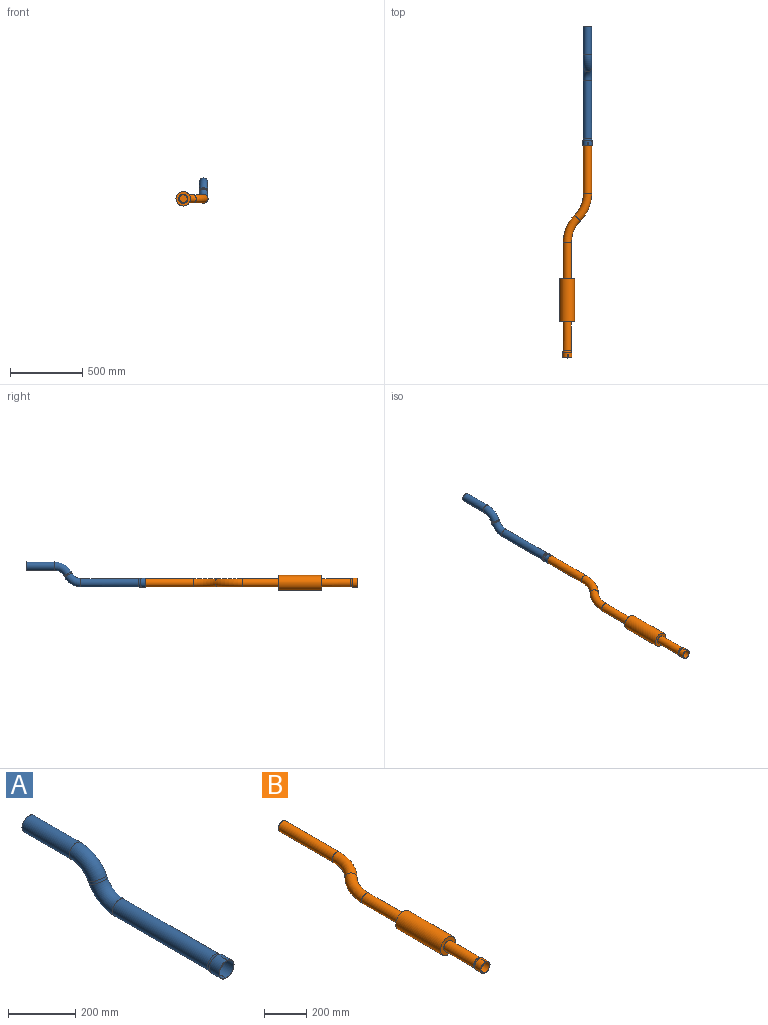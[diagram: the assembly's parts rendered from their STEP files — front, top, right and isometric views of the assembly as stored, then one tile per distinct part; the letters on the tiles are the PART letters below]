
ASSEMBLY  parts=2 mates=1
PART A: 23 faces, bbox 63x830x193.3 mm
  f0: cylinder r=30mm len=60mm, axis (0,1,0), area 7420.7mm2, adj f1,f2,f14,f17,f18,f19,f20,f21
  f1: plane 62.56x34.25mm, normal (0,-1,0), area 141.2mm2, adj f0,f16,f18,f20
  f2: plane 62.56x34.25mm, normal (0,-1,0), area 141.2mm2, adj f0,f16,f17,f21
  f3: cylinder r=27.07mm len=400mm, axis (0,1,0), area 68046.9mm2, adj f4,f14
  f4: torus R=100mm, axis (1,0,0), area 18541.2mm2, adj f3,f5
  f5: cylinder r=27.07mm len=54.15mm, axis (0,0.46,0.89), area 1441.6mm2, adj f4,f6
  f6: torus R=100mm, axis (-1,0,0), area 18541.2mm2, adj f5,f7
  f7: cylinder r=27.07mm len=198.76mm, axis (0,1,0), area 33813mm2, adj f6,f8
  f8: plane 57.15x57.15mm, normal (0,1,0), area 262.2mm2, adj f7,f13
  f9: cylinder r=28.57mm len=400mm, axis (0,1,0), area 71816.8mm2, adj f10,f15
  f10: torus R=100mm, axis (1,0,0), area 19568.4mm2, adj f9,f11
  f11: cylinder r=28.57mm len=57.15mm, axis (0,0.46,0.89), area 1521.5mm2, adj f10,f12
  f12: torus R=100mm, axis (-1,0,0), area 19568.4mm2, adj f11,f13
  f13: cylinder r=28.57mm len=198.76mm, axis (0,1,0), area 35686.3mm2, adj f8,f12
  f14: revolved ~60x60mm, area 1877.3mm2, adj f0,f3
  f15: revolved ~63x63mm, area 1977.9mm2, adj f9,f16
  f16: cylinder r=31.5mm len=63mm, axis (0,1,0), area 7791.8mm2, adj f1,f2,f15,f17,f18,f19,f20,f21
  f17: plane 25x1.48mm, normal (0.99,0,-0.17), area 37.5mm2, adj f0,f2,f16,f19
  f18: plane 25x1.49mm, normal (-1,0,0.09), area 37.5mm2, adj f0,f1,f16,f19
  f19: plane 2.61x1.8mm, normal (0,-1,0), area 3.7mm2, adj f0,f16,f17,f18
  f20: plane 25x1.48mm, normal (-0.99,0,0.17), area 37.5mm2, adj f0,f1,f16,f22
  f21: plane 25x1.49mm, normal (1,0,-0.09), area 37.5mm2, adj f0,f2,f16,f22
  f22: plane 2.61x1.8mm, normal (0,-1,0), area 3.7mm2, adj f0,f16,f20,f21
PART B: 28 faces, bbox 241.2x1500x101 mm
  f0: cylinder r=27.07mm len=250mm, axis (0,1,0), area 42529.3mm2, adj f2,f27
  f1: cylinder r=28.57mm len=250mm, axis (0,1,0), area 44885.5mm2, adj f6,f10
  f2: torus R=238.99mm, axis (0,0,-1), area 31932.1mm2, adj f0,f3
  f3: torus R=238.99mm, axis (0,0,1), area 31932.1mm2, adj f2,f4
  f4: cylinder r=27.07mm len=362.01mm, axis (0,1,0), area 61584.2mm2, adj f3,f5
  f5: plane 57.15x57.15mm, normal (0,1,0), area 262.2mm2, adj f4,f8
  f6: torus R=238.99mm, axis (0,0,-1), area 33701.1mm2, adj f1,f7
  f7: torus R=238.99mm, axis (0,0,1), area 33701.1mm2, adj f6,f8
  f8: cylinder r=28.57mm len=362.01mm, axis (0,1,0), area 64996mm2, adj f5,f7
  f9: plane 101x101mm, normal (0,-1,0), area 5446.6mm2, adj f11,f25
  f10: plane 101x101mm, normal (0,1,0), area 5446.6mm2, adj f1,f11
  f11: cylinder r=50.5mm len=300mm, axis (0,-1,0), area 95190.3mm2, adj f9,f10
  f12: plane 25x1.49mm, normal (1,0,-0.09), area 37.5mm2, adj f13,f19,f22,f23
  f13: plane 62.56x34.25mm, normal (0,-1,0), area 141.2mm2, adj f12,f14,f19,f23
  f14: plane 25x1.48mm, normal (0.99,0,-0.17), area 37.5mm2, adj f13,f15,f19,f23
  f15: plane 2.61x1.8mm, normal (0,-1,0), area 3.7mm2, adj f14,f16,f19,f23
  f16: plane 25x1.49mm, normal (-1,0,0.09), area 37.5mm2, adj f15,f17,f19,f23
  f17: plane 62.56x34.25mm, normal (0,-1,0), area 141.2mm2, adj f16,f18,f19,f23
  f18: plane 25x1.48mm, normal (-0.99,0,0.17), area 37.5mm2, adj f17,f19,f22,f23
  f19: cylinder r=30mm len=60mm, axis (0,1,0), area 7420.7mm2, adj f12,f13,f14,f15,f16,f17,f18,f20
  f20: revolved ~60x60mm, area 1877.3mm2, adj f19,f21
  f21: cylinder r=27.07mm len=200mm, axis (0,1,0), area 34023.4mm2, adj f20,f26
  f22: plane 2.61x1.8mm, normal (0,-1,0), area 3.7mm2, adj f12,f18,f19,f23
  f23: cylinder r=31.5mm len=63mm, axis (0,1,0), area 7791.8mm2, adj f12,f13,f14,f15,f16,f17,f18,f22
  f24: revolved ~63x63mm, area 1977.9mm2, adj f23,f25
  f25: cylinder r=28.57mm len=200mm, axis (0,1,0), area 35908.4mm2, adj f9,f24
  f26: plane 54.15x54.15mm, normal (0,-1,0), area 2303mm2, adj f21
  f27: plane 54.15x54.15mm, normal (0,1,0), area 2303mm2, adj f0
PLACE A t=(370.54,1121.23,268.76)mm
PLACE B t=(230.54,-348.15,268.76)mm fixed
MATE slider A.f0 <-> B.f4  axis (0,-1,0) through (370.54,1071.23,268.76)mm
